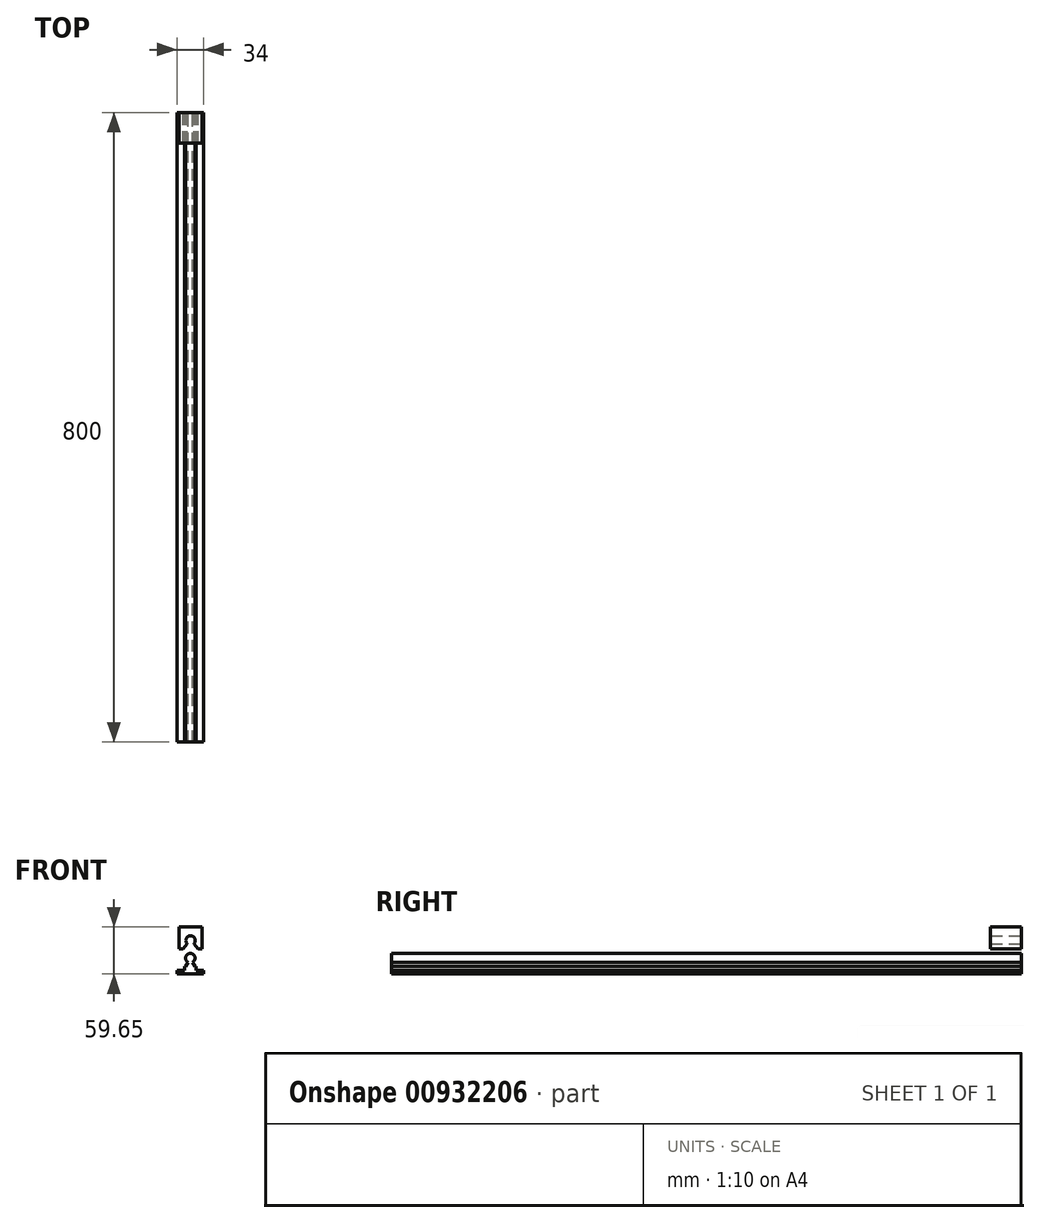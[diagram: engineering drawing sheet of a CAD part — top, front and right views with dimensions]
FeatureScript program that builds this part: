
annotation { "Feature Type Name" : "Feature", "Feature Type Description" : "" }
export const myFeature = defineFeature(function(context is Context, id is Id, definition is map)
    precondition{}
    {
        {
            var Q0;
            Q0=qCreatedBy(makeId("Front.planeOp"),FACE);
            var sketch = newSketch(context, id + "F0", { "sketchPlane" : qUnion([Q0])});
            skLineSegment(sketch, "E0", {"start": v(0, 0) * mm, "end": v(3, -5.2) * mm, "construction": true});
            skLineSegment(sketch, "E1", {"start": v(0, 0) * mm, "end": v(-3, -5.2) * mm, "construction": true});
            skLineSegment(sketch, "E2", {"start": v(-3, -5.2) * mm, "end": v(3, -5.2) * mm, "construction": true});
            skLineSegment(sketch, "E3", {"start": v(-3, -5.2) * mm, "end": v(-6, -10.4) * mm});
            skLineSegment(sketch, "E4", {"start": v(3, -5.2) * mm, "end": v(6, -10.4) * mm});
            skLineSegment(sketch, "E5", {"start": v(-6, -10.4) * mm, "end": v(6, -10.4) * mm, "construction": true});
            skLineSegment(sketch, "E6", {"start": v(0, -10.4) * mm, "end": v(0, -5.2) * mm, "construction": true});
            skLineSegment(sketch, "E7", {"start": v(0, -20.2) * mm, "end": v(0, -10.4) * mm, "construction": true});
            skLineSegment(sketch, "E8", {"start": v(6, -10.4) * mm, "end": v(7.5, -10.4) * mm});
            skLineSegment(sketch, "E9", {"start": v(-6, -10.4) * mm, "end": v(-7.5, -10.4) * mm});
            skLineSegment(sketch, "E10", {"start": v(-17, -20.2) * mm, "end": v(17, -20.2) * mm});
            skLineSegment(sketch, "E11", {"start": v(-17, -20.2) * mm, "end": v(-17, -15.7) * mm});
            skLineSegment(sketch, "E12", {"start": v(17, -20.2) * mm, "end": v(17, -15.7) * mm});
            skLineSegment(sketch, "E13", {"start": v(17, -15.7) * mm, "end": v(7.5, -15.7) * mm});
            skLineSegment(sketch, "E14", {"start": v(7.5, -15.7) * mm, "end": v(7.5, -10.4) * mm});
            skLineSegment(sketch, "E15", {"start": v(-17, -15.7) * mm, "end": v(-7.5, -15.7) * mm});
            skLineSegment(sketch, "E16", {"start": v(-7.5, -15.7) * mm, "end": v(-7.5, -10.4) * mm});
            skArc(sketch, "E17", {"start": v(-3, -5.2) * mm, "mid": v(0, -6) * mm, "end": v(3, -5.2) * mm, "construction": true});
            skArc(sketch, "E18", {"start": v(3, -5.2) * mm, "mid": v(0, 6) * mm, "end": v(-3, -5.2) * mm});
            skLineSegment(sketch, "E19", {"start": v(-14.13, 39.45) * mm, "end": v(14.79, 39.45) * mm});
            skLineSegment(sketch, "E20", {"start": v(14.79, 39.45) * mm, "end": v(14.79, 11.85) * mm});
            skLineSegment(sketch, "E21", {"start": v(-14.13, 39.45) * mm, "end": v(-14.13, 11.85) * mm});
            skLineSegment(sketch, "E22", {"start": v(-14.13, 11.85) * mm, "end": v(-9.26, 11.85) * mm});
            skLineSegment(sketch, "E23", {"start": v(0.33, 39.45) * mm, "end": v(0.33, 22.45) * mm, "construction": true});
            skLineSegment(sketch, "E24", {"start": v(-3.92, 18.22) * mm, "end": v(4.58, 18.22) * mm, "construction": true});
            skLineSegment(sketch, "E25", {"start": v(4.58, 18.22) * mm, "end": v(9.92, 11.85) * mm});
            skLineSegment(sketch, "E26", {"start": v(-3.92, 18.22) * mm, "end": v(-9.26, 11.85) * mm});
            skArc(sketch, "E27", {"start": v(-3.92, 18.22) * mm, "mid": v(0.33, 16.45) * mm, "end": v(4.58, 18.22) * mm, "construction": true});
            skArc(sketch, "E28", {"start": v(4.58, 18.22) * mm, "mid": v(0.33, 28.45) * mm, "end": v(-3.92, 18.22) * mm});
            skLineSegment(sketch, "E29", {"start": v(-9.26, 11.85) * mm, "end": v(9.92, 11.85) * mm, "construction": true});
            skLineSegment(sketch, "E30", {"start": v(9.92, 11.85) * mm, "end": v(14.79, 11.85) * mm});
            skSolve(sketch);
        }
        {
            var Q0;
            Q0=makeQuery(id+"F0.imprint","IMPRINT",FACE,{"disambiguationData":[TD([[makeQuery(id+"F0.imprint","IMPRINT",EDGE,{"derivedFrom":sQuery(id+"F0.wireOp",EDGE,"E3")}),1.0]])]});
            extrude(context, id + "F1", {"entities" : qUnion([Q0]), "depth" : 800 * mm, "offsetDistance" : 25 * mm});
        }
        {
            var Q0;
            Q0=makeQuery(id+"F0.imprint","IMPRINT",FACE,{"disambiguationData":[TD([[makeQuery(id+"F0.imprint","IMPRINT",EDGE,{"derivedFrom":sQuery(id+"F0.wireOp",EDGE,"E19")}),-1.0]])]});
            extrude(context, id + "F2", {"entities" : qUnion([Q0]), "depth" : 39 * mm, "offsetDistance" : 25 * mm});
        }
    });
